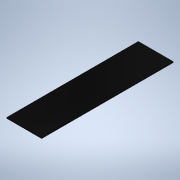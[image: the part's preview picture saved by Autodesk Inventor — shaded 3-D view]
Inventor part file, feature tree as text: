
AUTODESK INVENTOR PART (.ipt)
format: ipt  version: 2022 (Build 260153000, 153)  size: 105,984 bytes
history: native  units: mm
features: sketch x2, other x1, extrude x1, hole x1
ambient origin geometry x8: Origin, YZ Plane, XZ Plane, XY Plane, X Axis, Y Axis, Z Axis, Center Point
bodies: Body1 (feature_tree)
feature tree (5):
  other  "ソリッド1"
  extrude  "押し出し1"  Depth=200.0mm
  hole  "穴1"  [1 undecoded]
  sketch  "スケッチ1"
  sketch  "スケッチ3"
note: 1 required parameter value undecoded (feature->parameter linkage not recoverable at this tier; creation-order binding heuristic only, values carry confidence <= 0.55)
